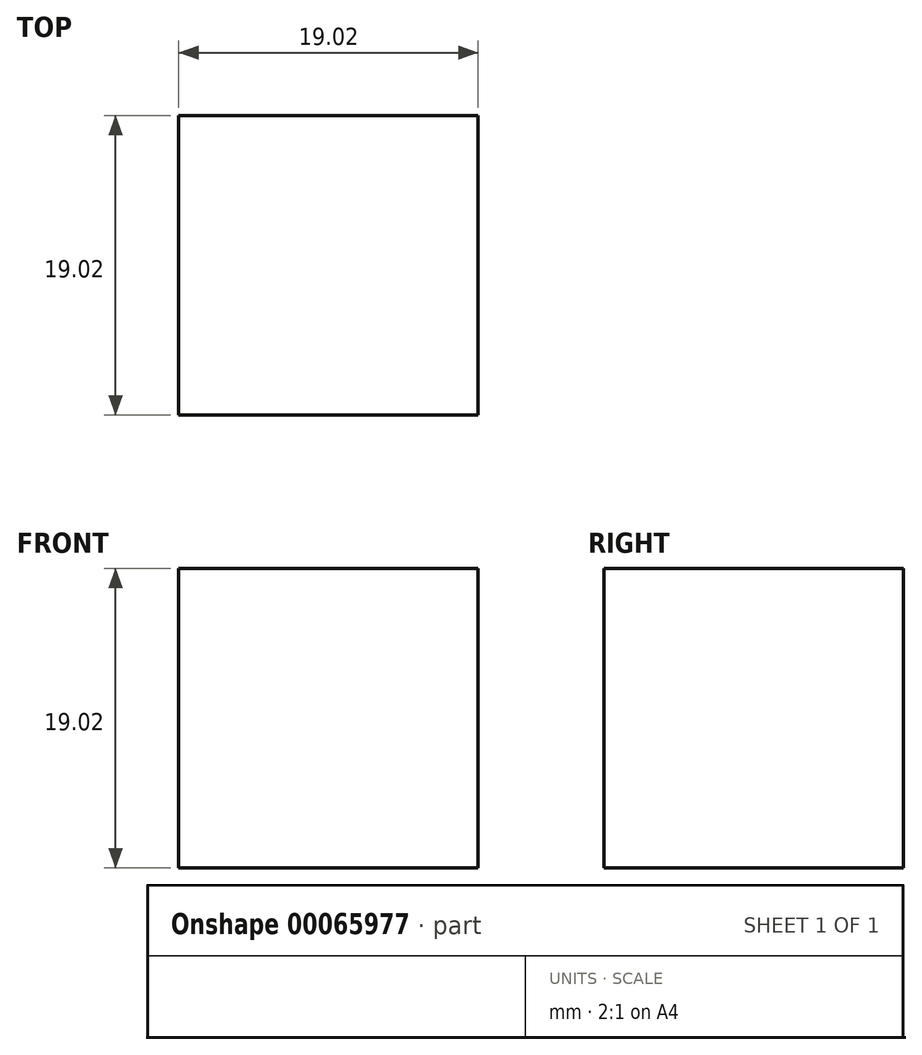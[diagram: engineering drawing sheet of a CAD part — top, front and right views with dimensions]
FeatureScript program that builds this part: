
annotation { "Feature Type Name" : "Feature", "Feature Type Description" : "" }
export const myFeature = defineFeature(function(context is Context, id is Id, definition is map)
    precondition{}
    {
        {
            var Q0;
            Q0=qCreatedBy(makeId("Top.planeOp"),FACE);
            var sketch = newSketch(context, id + "F0", { "sketchPlane" : qUnion([Q0])});
            skLineSegment(sketch, "E0.bottom", {"start": v(0, 0) * mm, "end": v(0, 0) * mm});
            skLineSegment(sketch, "E0.top", {"start": v(0, 0) * mm, "end": v(0, 0) * mm});
            skLineSegment(sketch, "E0.left", {"start": v(0, 0) * mm, "end": v(0, 0) * mm});
            skLineSegment(sketch, "E0.right", {"start": v(0, 0) * mm, "end": v(0, 0) * mm});
            skLineSegment(sketch, "E1.bottom", {"start": v(0, 0) * mm, "end": v(19.02, 0) * mm});
            skLineSegment(sketch, "E1.top", {"start": v(0, -19.02) * mm, "end": v(19.02, -19.02) * mm});
            skLineSegment(sketch, "E1.left", {"start": v(0, 0) * mm, "end": v(0, -19.02) * mm});
            skLineSegment(sketch, "E1.right", {"start": v(19.02, 0) * mm, "end": v(19.02, -19.02) * mm});
            skSolve(sketch);
        }
        {
            var Q0;
            Q0=makeQuery(id+"F0.imprint","IMPRINT",FACE,{"disambiguationData":[TD([[makeQuery(id+"F0.imprint","IMPRINT",EDGE,{"derivedFrom":sQuery(id+"F0.wireOp",EDGE,"E1.bottom")}),-1.0]])]});
            extrude(context, id + "F1", {"entities" : qUnion([Q0]), "depth" : 19.02 * mm});
        }
    });
